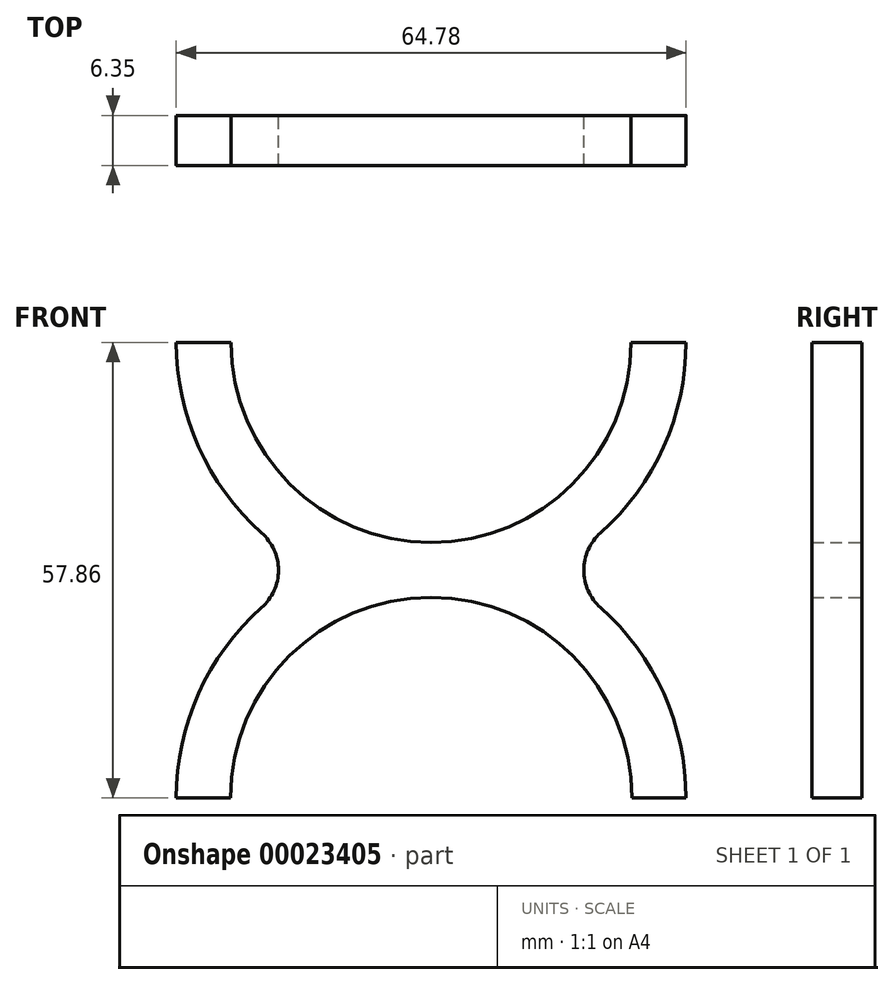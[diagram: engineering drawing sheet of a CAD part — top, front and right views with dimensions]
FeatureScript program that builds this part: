
annotation { "Feature Type Name" : "Feature", "Feature Type Description" : "" }
export const myFeature = defineFeature(function(context is Context, id is Id, definition is map)
    precondition{}
    {
        {
            var Q0;
            Q0=qCreatedBy(makeId("Front.planeOp"),FACE);
            var sketch = newSketch(context, id + "F0", { "sketchPlane" : qUnion([Q0])});
            skArc(sketch, "E0", {"start": v(25.49, -25.49) * mm, "mid": v(0, 0) * mm, "end": v(-25.49, -25.49) * mm});
            skPoint(sketch, "E1.center.orphan", {"position": v(0, 0) * mm});
            skArc(sketch, "E2", {"start": v(32.39, -25.49) * mm, "mid": v(29.55, -12.23) * mm, "end": v(21.53, -1.3) * mm});
            skArc(sketch, "E3", {"start": v(-32.37, 32.37) * mm, "mid": v(-29.54, 19.12) * mm, "end": v(-21.53, 8.2) * mm});
            skPoint(sketch, "E4.center.orphan", {"position": v(0, 25.49) * mm});
            skArc(sketch, "E5", {"start": v(-25.4, 32.37) * mm, "mid": v(0, 6.97) * mm, "end": v(25.4, 32.37) * mm});
            skLineSegment(sketch, "E6", {"start": v(25.49, -25.49) * mm, "end": v(32.39, -25.49) * mm});
            skLineSegment(sketch, "E7", {"start": v(32.39, -25.49) * mm, "end": v(25.49, -25.49) * mm});
            skLineSegment(sketch, "E8", {"start": v(25.4, 32.37) * mm, "end": v(32.37, 32.37) * mm});
            skLineSegment(sketch, "E9", {"start": v(32.37, 32.37) * mm, "end": v(25.4, 32.37) * mm});
            skLineSegment(sketch, "E10.trimOffspring", {"start": v(-25.4, 32.37) * mm, "end": v(-32.37, 32.37) * mm});
            skLineSegment(sketch, "E11.trimOffspring", {"start": v(-25.49, -25.49) * mm, "end": v(-32.39, -25.49) * mm});
            skArc(sketch, "E12.trimOffspring", {"start": v(-21.53, -1.3) * mm, "mid": v(-29.55, -12.23) * mm, "end": v(-32.38, -25.49) * mm});
            skArc(sketch, "E13.trimOffspring", {"start": v(21.53, 8.2) * mm, "mid": v(29.54, 19.12) * mm, "end": v(32.37, 32.37) * mm});
            skPoint(sketch, "E14.visualSharp", {"position": v(-14.54, 3.45) * mm});
            skArc(sketch, "E14.filletArc", {"start": v(-21.53, -1.3) * mm, "mid": v(-19.4, 3.45) * mm, "end": v(-21.53, 8.2) * mm});
            skPoint(sketch, "E15.visualSharp", {"position": v(14.54, 3.45) * mm});
            skArc(sketch, "E15.filletArc", {"start": v(21.53, 8.2) * mm, "mid": v(19.4, 3.45) * mm, "end": v(21.53, -1.3) * mm});
            skSolve(sketch);
        }
        {
            var Q0;
            Q0=makeQuery(id+"F0.imprint","IMPRINT",FACE,{"disambiguationData":[TD([[makeQuery(id+"F0.imprint","IMPRINT",EDGE,{"derivedFrom":sQuery(id+"F0.wireOp",EDGE,"E0")}),-1.0]])]});
            extrude(context, id + "F1", {"entities" : qUnion([Q0]), "depth" : 6.35 * mm});
        }
    });
